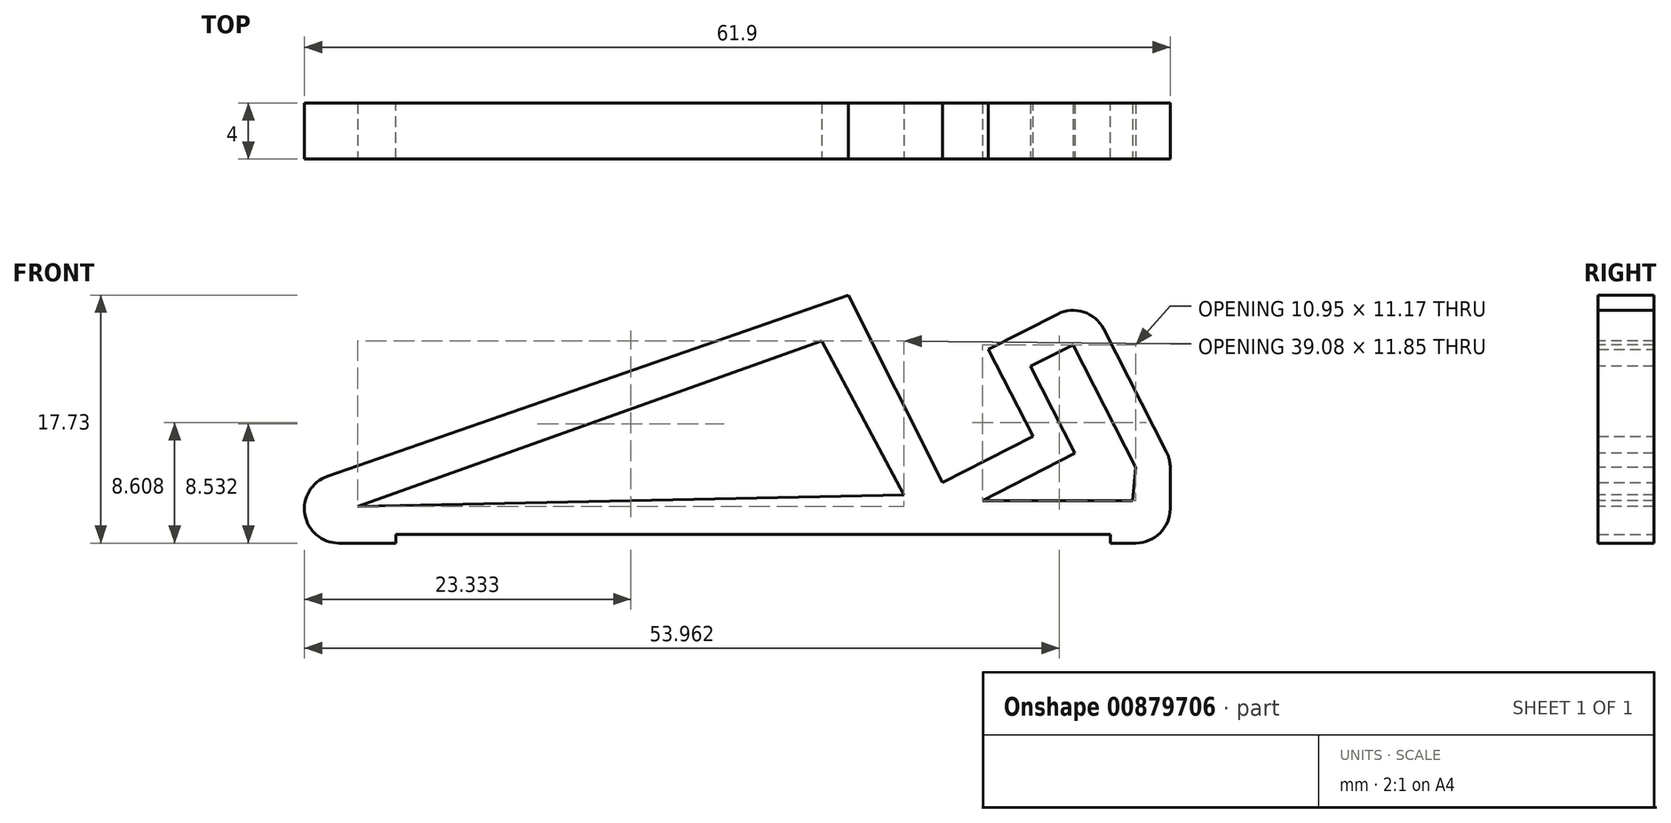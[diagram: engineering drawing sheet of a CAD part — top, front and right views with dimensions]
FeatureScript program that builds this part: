
annotation { "Feature Type Name" : "Feature", "Feature Type Description" : "" }
export const myFeature = defineFeature(function(context is Context, id is Id, definition is map)
    precondition{}
    {
        {
            var Q0;
            Q0=qCreatedBy(makeId("Front.planeOp"),FACE);
            var sketch = newSketch(context, id + "F0", { "sketchPlane" : qUnion([Q0])});
            skLineSegment(sketch, "E0", {"start": v(-13.48, 0) * mm, "end": v(43.5, 0) * mm});
            skLineSegment(sketch, "E1", {"start": v(45.97, 2.46) * mm, "end": v(45.97, 5.4) * mm});
            skLineSegment(sketch, "E2", {"start": v(45.7, 6.53) * mm, "end": v(41.2, 15.31) * mm});
            skLineSegment(sketch, "E3", {"start": v(37.9, 16.38) * mm, "end": v(32.97, 13.86) * mm});
            skLineSegment(sketch, "E4", {"start": v(32.97, 13.86) * mm, "end": v(36.15, 7.63) * mm});
            skLineSegment(sketch, "E5", {"start": v(36.15, 7.63) * mm, "end": v(29.7, 4.33) * mm});
            skLineSegment(sketch, "E6", {"start": v(29.7, 4.33) * mm, "end": v(22.97, 17.73) * mm});
            skLineSegment(sketch, "E7", {"start": v(22.97, 17.73) * mm, "end": v(-14.28, 4.78) * mm});
            skLineSegment(sketch, "E8.bottom", {"start": v(-9.39, -0.93) * mm, "end": v(41.69, -0.93) * mm});
            skLineSegment(sketch, "E8.top", {"start": v(-9.39, 0.62) * mm, "end": v(41.69, 0.62) * mm});
            skLineSegment(sketch, "E8.left", {"start": v(-9.39, -0.93) * mm, "end": v(-9.39, 0.62) * mm});
            skLineSegment(sketch, "E8.right", {"start": v(41.69, -0.93) * mm, "end": v(41.69, 0.62) * mm});
            skPoint(sketch, "E9.visualSharp", {"position": v(-28.03, 0) * mm});
            skArc(sketch, "E9.filletArc", {"start": v(-14.28, 4.78) * mm, "mid": v(-15.9, 2.05) * mm, "end": v(-13.48, 0) * mm});
            skPoint(sketch, "E10.visualSharp", {"position": v(40.1, 17.5) * mm});
            skArc(sketch, "E10.filletArc", {"start": v(41.2, 15.31) * mm, "mid": v(39.78, 16.53) * mm, "end": v(37.9, 16.38) * mm});
            skPoint(sketch, "E11.visualSharp", {"position": v(45.97, 6) * mm});
            skArc(sketch, "E11.filletArc", {"start": v(45.97, 5.4) * mm, "mid": v(45.9, 5.98) * mm, "end": v(45.7, 6.53) * mm});
            skPoint(sketch, "E12.visualSharp", {"position": v(45.97, 0) * mm});
            skArc(sketch, "E12.filletArc", {"start": v(43.5, 0) * mm, "mid": v(45.25, 0.72) * mm, "end": v(45.97, 2.46) * mm});
            skSolve(sketch);
        }
        {
            var Q0;
            Q0=makeQuery(id+"F0.imprint","IMPRINT",FACE,{"disambiguationData":[TD([[makeQuery(id+"F0.imprint","IMPRINT",EDGE,{"derivedFrom":sQuery(id+"F0.wireOp",EDGE,"E1")}),1.0]])]});
            extrude(context, id + "F1", {"entities" : qUnion([Q0]), "depth" : 4 * mm, "offsetDistance" : 25 * mm});
        }
        {
            var Q0;
            Q0=makeQuery(id+"F1.opExtrude","CAP_FACE",FACE,{"disambiguationData":[OSD([sQuery(id+"F0.wireOp",EDGE,"E0"),sQuery(id+"F0.wireOp",EDGE,"E1"),sQuery(id+"F0.wireOp",EDGE,"E2"),sQuery(id+"F0.wireOp",EDGE,"E3"),sQuery(id+"F0.wireOp",EDGE,"E4"),sQuery(id+"F0.wireOp",EDGE,"E5"),sQuery(id+"F0.wireOp",EDGE,"E6"),sQuery(id+"F0.wireOp",EDGE,"E7"),sQuery(id+"F0.wireOp",EDGE,"E8.top"),sQuery(id+"F0.wireOp",EDGE,"E8.left"),sQuery(id+"F0.wireOp",EDGE,"E8.right"),sQuery(id+"F0.wireOp",EDGE,"E9.filletArc"),sQuery(id+"F0.wireOp",EDGE,"E10.filletArc"),sQuery(id+"F0.wireOp",EDGE,"E11.filletArc"),sQuery(id+"F0.wireOp",EDGE,"E12.filletArc")])],"isStart":false});
            var sketch = newSketch(context, id + "F2", { "sketchPlane" : qUnion([Q0])});
            skLineSegment(sketch, "E13", {"start": v(-12.14, 2.6) * mm, "end": v(21.04, 14.46) * mm});
            skLineSegment(sketch, "E14", {"start": v(21.04, 14.46) * mm, "end": v(26.94, 3.43) * mm});
            skLineSegment(sketch, "E15", {"start": v(26.94, 3.43) * mm, "end": v(-12.14, 2.6) * mm});
            skLineSegment(sketch, "E16", {"start": v(32.56, 3.02) * mm, "end": v(43.28, 3.02) * mm});
            skLineSegment(sketch, "E17", {"start": v(43.28, 3.02) * mm, "end": v(43.5, 5.4) * mm});
            skLineSegment(sketch, "E18", {"start": v(43.5, 5.4) * mm, "end": v(39.02, 14.2) * mm});
            skLineSegment(sketch, "E19", {"start": v(39.02, 14.2) * mm, "end": v(35.99, 12.64) * mm});
            skLineSegment(sketch, "E20", {"start": v(35.99, 12.64) * mm, "end": v(39.16, 6.43) * mm});
            skLineSegment(sketch, "E21", {"start": v(39.16, 6.43) * mm, "end": v(32.56, 3.02) * mm});
            skSolve(sketch);
        }
        {
            var Q0;
            Q0=makeQuery(id+"F2.imprint","IMPRINT",FACE,{"disambiguationData":[TD([[makeQuery(id+"F2.imprint","IMPRINT",EDGE,{"derivedFrom":sQuery(id+"F2.wireOp",EDGE,"E13")}),-1.0]])]});
            var Q1;
            Q1=makeQuery(id+"F2.imprint","IMPRINT",FACE,{"disambiguationData":[TD([[makeQuery(id+"F2.imprint","IMPRINT",EDGE,{"derivedFrom":sQuery(id+"F2.wireOp",EDGE,"E16")}),1.0]])]});
            extrude(context, id + "F3", {"entities" : qUnion([Q0, Q1]), "operationType" : NewBodyOperationType.REMOVE, "endBound" : BoundingType.UP_TO_NEXT, "oppositeDirection" : true, "depth" : 25 * mm, "offsetDistance" : 25 * mm});
        }
    });
